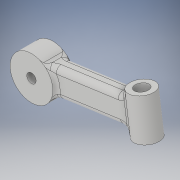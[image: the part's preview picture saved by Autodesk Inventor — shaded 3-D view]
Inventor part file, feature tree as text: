
AUTODESK INVENTOR PART (.ipt)
format: ipt  version: 2018 (Build 220112000, 112)  size: 306,688 bytes
history: native  units: in
note: dims shown in document units (in); Inventor stores cm internally (conversion verified against a paired STEP export)
features: fillet x3, sketch x3, extrude x2, revolve x1
ambient origin geometry x8: Origin, YZ Plane, XZ Plane, XY Plane, X Axis, Y Axis, Z Axis, Center Point
bodies: Solid1 (feature_tree)
feature tree (9):
  extrude  "Extrusion1"  Depth=0.6299in
  extrude  "Extrusion2"  Depth=1.1811in
  revolve  "Revolution1"  [1 undecoded]
  fillet  "Fillet1"  Radius=0.5906in
  fillet  "Fillet2"  Radius=0.0787in
  fillet  "Fillet3"  Radius=0.0492in
  sketch  "Sketch1"  dims[d0=0.1378in d1=0.6299in]
  sketch  "Sketch2"  dims[d2=0.315in d3=0.0in d4=1.1811in]
  sketch  "Sketch3"  dims[d5=0.2362in d6=0.0in d7=0.3937in d8=0.5906in d9=0.0787in d10=0.0492in d11=0.0984in d12=0.0984in d13=90.0deg d14=0.0787in d15=0.0787in d16=0.0787in]
note: 1 required parameter value undecoded (feature->parameter linkage not recoverable at this tier; creation-order binding heuristic only, values carry confidence <= 0.55)
